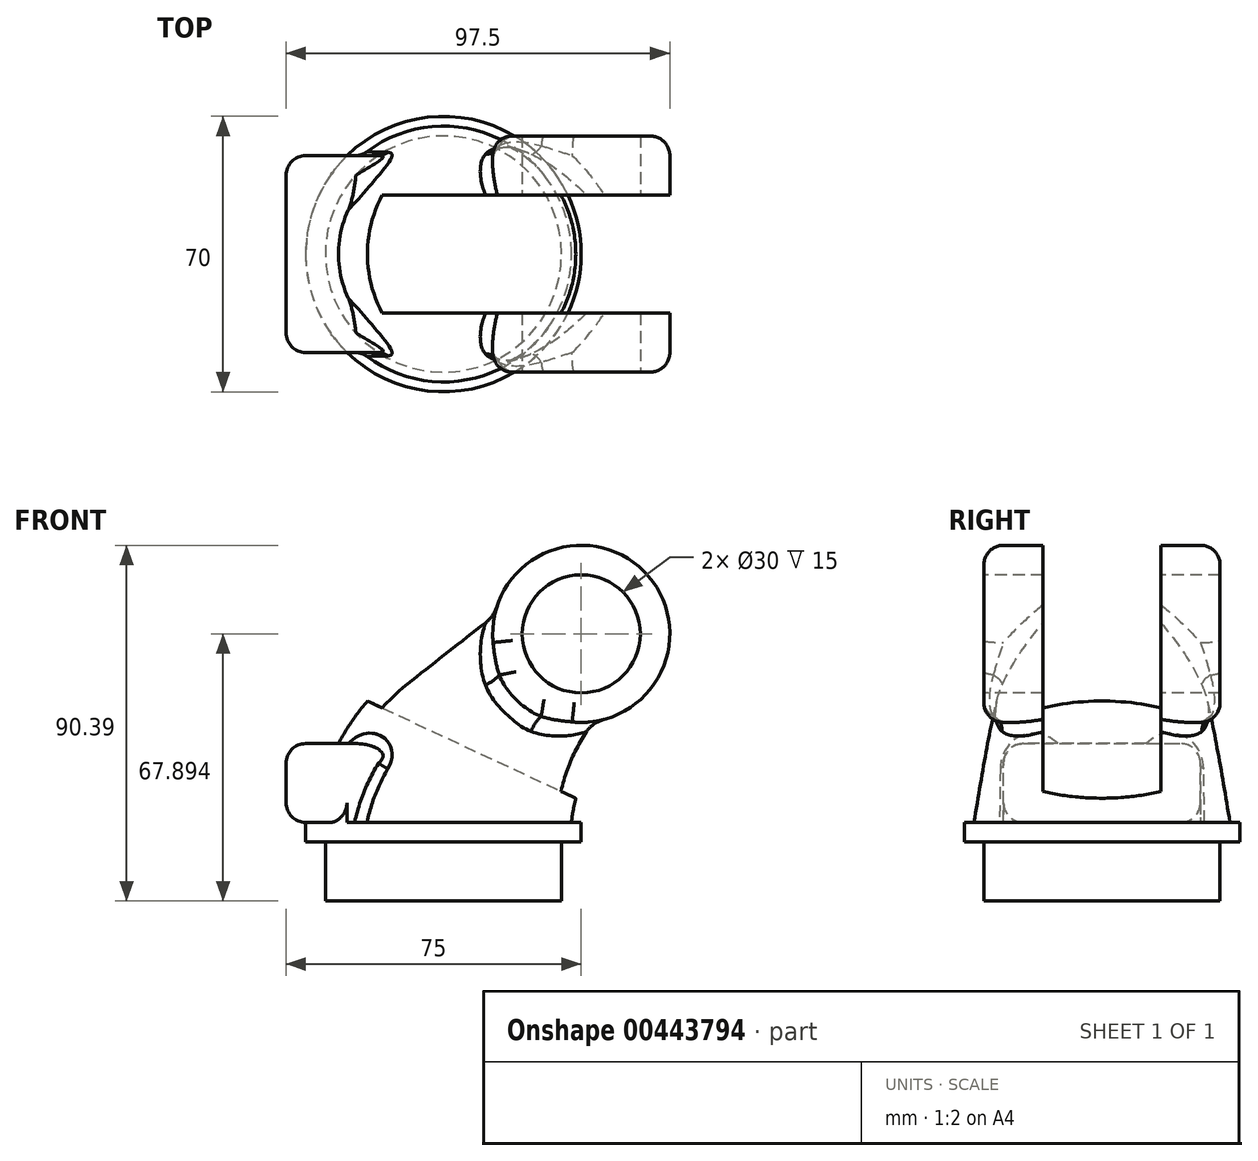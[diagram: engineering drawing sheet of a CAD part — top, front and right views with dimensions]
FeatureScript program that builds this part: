
annotation { "Feature Type Name" : "Feature", "Feature Type Description" : "" }
export const myFeature = defineFeature(function(context is Context, id is Id, definition is map)
    precondition{}
    {
        {
            var Q0;
            Q0=qCreatedBy(makeId("Top.planeOp"),FACE);
            var sketch = newSketch(context, id + "F0", { "sketchPlane" : qUnion([Q0])});
            skCircle(sketch, "E0", {"center": v(0, 0) * mm, "radius": 35 * mm});
            skSolve(sketch);
        }
        {
            var Q0;
            Q0 = qSketchRegion(id + "F0", true);
            extrude(context, id + "F1", {"entities" : qUnion([Q0]), "depth" : 5 * mm});
        }
        {
            var Q0;
            Q0=qCreatedBy(makeId("Front.planeOp"),FACE);
            var sketch = newSketch(context, id + "F2", { "sketchPlane" : qUnion([Q0])});
            skArc(sketch, "E1", {"start": v(17.6, 38.3) * mm, "mid": v(5.55, 23.37) * mm, "end": v(0, 5) * mm});
            skLineSegment(sketch, "E2", {"start": v(35, 52.9) * mm, "end": v(17.6, 38.3) * mm});
            skSolve(sketch);
        }
        {
            var Q0;
            Q0=sQuery(id+"F2.wireOp",EDGE,"E2");
            var Q1;
            Q1=sQuery(id+"F2.wireOp",VERTEX,"E2.start");
            cPlane(context, id + "F3", {"entities" : qUnion([Q0, Q1]), "cplaneType" : CPlaneType.LINE_POINT, "offset" : 25 * mm, "width" : 150 * mm, "height" : 150 * mm});
        }
        {
            var Q0;
            Q0=qCreatedBy(id+"F3.planeOp",FACE);
            var sketch = newSketch(context, id + "F4", { "sketchPlane" : qUnion([Q0])});
            skCircle(sketch, "E3", {"center": v(0, 18.02) * mm, "radius": 22.5 * mm});
            skSolve(sketch);
        }
        {
            var Q0;
            Q0=makeQuery(id+"F1.opExtrude","CAP_FACE",FACE,{"disambiguationData":[OSD([sQuery(id+"F0.wireOp",EDGE,"E0")])],"isStart":false});
            var sketch = newSketch(context, id + "F5", { "sketchPlane" : qUnion([Q0])});
            skCircle(sketch, "E4", {"center": v(0, 0) * mm, "radius": 32.5 * mm});
            skSolve(sketch);
        }
        {
            var Q0;
            Q0=qCreatedBy(makeId("Front.planeOp"),FACE);
            var sketch = newSketch(context, id + "F6", { "sketchPlane" : qUnion([Q0])});
            skArc(sketch, "E5", {"start": v(-13.25, 41.78) * mm, "mid": v(-26.5, 25.3) * mm, "end": v(-32.5, 5) * mm});
            skLineSegment(sketch, "E6", {"start": v(-13.25, 41.78) * mm, "end": v(20.54, 70.13) * mm});
            skSolve(sketch);
        }
        {
            var Q0;
            Q0=qCreatedBy(makeId("Front.planeOp"),FACE);
            var sketch = newSketch(context, id + "F7", { "sketchPlane" : qUnion([Q0])});
            skArc(sketch, "E7", {"start": v(48.46, 34.82) * mm, "mid": v(37.6, 21.45) * mm, "end": v(32.5, 5) * mm});
            skLineSegment(sketch, "E8", {"start": v(48.46, 34.82) * mm, "end": v(49.46, 35.66) * mm});
            skSolve(sketch);
        }
        {
            var Q1;
            Q1=makeQuery(id+"F5.imprint","IMPRINT",FACE,{"disambiguationData":[TD([[makeQuery(id+"F5.imprint","IMPRINT",EDGE,{"derivedFrom":sQuery(id+"F5.wireOp",EDGE,"E4")}),1.0]])]});
            var Q2;
            Q2=makeQuery(id+"F4.imprint","IMPRINT",FACE,{"disambiguationData":[TD([[makeQuery(id+"F4.imprint","IMPRINT",EDGE,{"derivedFrom":sQuery(id+"F4.wireOp",EDGE,"E3")}),1.0]])]});
            var Q3;
            Q3 = qConstructionFilter(qBodyType(qCreatedBy(id + "F7" ,EDGE), BodyType.WIRE), ConstructionObject.NO);
            var Q4;
            Q4 = qConstructionFilter(qBodyType(qCreatedBy(id + "F6" ,EDGE), BodyType.WIRE), ConstructionObject.NO);
            loft(context, id + "F8", {"operationType" : NewBodyOperationType.ADD, "addGuides" : true, "sheetProfilesArray" : [{ "sheetProfileEntities" : qUnion([Q1]) }, { "sheetProfileEntities" : qUnion([Q2]) }], "guidesArray" : [{ "guideEntities" : qUnion([Q3]), "guideDerivativeType" : LoftGuideDerivativeType.DEFAULT, "guideDerivativeMagnitude" : 1 }, { "guideEntities" : qUnion([Q4]), "guideDerivativeType" : LoftGuideDerivativeType.DEFAULT, "guideDerivativeMagnitude" : 1 }]});
        }
        {
            var Q0;
            Q0=qCreatedBy(makeId("Front.planeOp"),FACE);
            var sketch = newSketch(context, id + "F9", { "sketchPlane" : qUnion([Q0])});
            skCircle(sketch, "E9", {"center": v(35, 52.9) * mm, "radius": 22.5 * mm});
            skSolve(sketch);
        }
        {
            var Q0;
            Q0 = qSketchRegion(id + "F9", true);
            extrude(context, id + "F10", {"entities" : qUnion([Q0]), "operationType" : NewBodyOperationType.ADD, "endBound" : BoundingType.SYMMETRIC, "depth" : 60 * mm});
        }
        {
            var Q0;
            Q0=makeQuery(id+"F10.boolean.opBoolean","INTERSECT",EDGE,{"disambiguationData":[OD(1.0)],"derivedFrom":[makeQuery(id+"F8.opLoft","SWEPT_FACE",FACE,{"disambiguationData":[OSD([sQuery(id+"F4.wireOp",EDGE,"E3"),sQuery(id+"F5.wireOp",EDGE,"E4"),sQuery(id+"F6.wireOp",VERTEX,"E6.start"),sQuery(id+"F6.wireOp",EDGE,"E5"),sQuery(id+"F6.wireOp",EDGE,"E6"),sQuery(id+"F7.wireOp",VERTEX,"E8.start"),sQuery(id+"F7.wireOp",EDGE,"E7"),sQuery(id+"F7.wireOp",EDGE,"E8")])]}),makeQuery(id+"F10.opExtrude","SWEPT_FACE",FACE,{"disambiguationData":[OSD([sQuery(id+"F9.wireOp",EDGE,"E9")])]})]});
            var Q1;
            Q1=makeQuery(id+"F10.boolean.opBoolean","INTERSECT",EDGE,{"disambiguationData":[OD(0.0)],"derivedFrom":[makeQuery(id+"F8.opLoft","SWEPT_FACE",FACE,{"disambiguationData":[OSD([sQuery(id+"F4.wireOp",EDGE,"E3"),sQuery(id+"F5.wireOp",EDGE,"E4"),sQuery(id+"F6.wireOp",VERTEX,"E6.start"),sQuery(id+"F6.wireOp",EDGE,"E5"),sQuery(id+"F6.wireOp",EDGE,"E6"),sQuery(id+"F7.wireOp",VERTEX,"E8.start"),sQuery(id+"F7.wireOp",EDGE,"E7"),sQuery(id+"F7.wireOp",EDGE,"E8")])]}),makeQuery(id+"F10.opExtrude","SWEPT_FACE",FACE,{"disambiguationData":[OSD([sQuery(id+"F9.wireOp",EDGE,"E9")])]})]});
            fillet(context, id + "F11", {"entities" : qUnion([Q0, Q1]), "radius" : 5 * mm, "tangentPropagation" : true, "allowEdgeOverflow" : false});
        }
        {
            var Q0;
            Q0=makeQuery(id+"F10.opExtrude","CAP_EDGE",EDGE,{"disambiguationData":[OSD([sQuery(id+"F9.wireOp",EDGE,"E9")])],"isStart":false});
            var Q1;
            Q1=makeQuery(id+"F10.opExtrude","CAP_EDGE",EDGE,{"disambiguationData":[OSD([sQuery(id+"F9.wireOp",EDGE,"E9")])],"isStart":true});
            fillet(context, id + "F12", {"entities" : qUnion([Q0, Q1]), "radius" : 5 * mm, "tangentPropagation" : true, "allowEdgeOverflow" : false});
        }
        {
            var Q0;
            Q0=makeQuery(id+"F10.opExtrude","CAP_FACE",FACE,{"disambiguationData":[OSD([sQuery(id+"F9.wireOp",EDGE,"E9")])],"isStart":false});
            var sketch = newSketch(context, id + "F13", { "sketchPlane" : qUnion([Q0])});
            skCircle(sketch, "E10", {"center": v(35, 52.9) * mm, "radius": 15 * mm});
            skSolve(sketch);
        }
        {
            var Q0;
            Q0 = qSketchRegion(id + "F13", true);
            extrude(context, id + "F14", {"entities" : qUnion([Q0]), "operationType" : NewBodyOperationType.REMOVE, "endBound" : BoundingType.THROUGH_ALL, "oppositeDirection" : true, "depth" : 25 * mm});
        }
        {
            var Q0;
            Q0=qCreatedBy(makeId("Front.planeOp"),FACE);
            var sketch = newSketch(context, id + "F15", { "sketchPlane" : qUnion([Q0])});
            skLineSegment(sketch, "E11", {"start": v(-104.18, 75.4) * mm, "end": v(57.5, 0) * mm});
            skLineSegment(sketch, "E12", {"start": v(57.5, 75.4) * mm, "end": v(57.5, 0) * mm});
            skLineSegment(sketch, "E13", {"start": v(-104.18, 75.4) * mm, "end": v(57.5, 75.4) * mm});
            skSolve(sketch);
        }
        {
            var Q0;
            Q0 = qSketchRegion(id + "F15", true);
            extrude(context, id + "F16", {"entities" : qUnion([Q0]), "operationType" : NewBodyOperationType.REMOVE, "endBound" : BoundingType.SYMMETRIC, "oppositeDirection" : true, "depth" : 30 * mm});
        }
        {
            var Q0;
            Q0=qCreatedBy(makeId("Front.planeOp"),FACE);
            var sketch = newSketch(context, id + "F17", { "sketchPlane" : qUnion([Q0])});
            skLineSegment(sketch, "E14.bottom", {"start": v(0, 0) * mm, "end": v(-30, 0) * mm});
            skLineSegment(sketch, "E14.top", {"start": v(0, -15) * mm, "end": v(-30, -15) * mm});
            skLineSegment(sketch, "E14.left", {"start": v(0, 0) * mm, "end": v(0, -15) * mm});
            skLineSegment(sketch, "E14.right", {"start": v(-30, 0) * mm, "end": v(-30, -15) * mm});
            skSolve(sketch);
        }
        {
            var Q0;
            Q0 = qSketchRegion(id + "F17", true);
            var Q1;
            Q1=sQuery(id+"F17.wireOp",EDGE,"E14.left");
            revolve(context, id + "F18", {"operationType" : NewBodyOperationType.ADD, "entities" : qUnion([Q0]), "axis" : qUnion([Q1]), "revolveType" : RevolveType.FULL});
        }
        {
            var Q0;
            Q0=qCreatedBy(makeId("Right.planeOp"),FACE);
            var sketch = newSketch(context, id + "F19", { "sketchPlane" : qUnion([Q0])});
            skLineSegment(sketch, "E15.bottom", {"start": v(-25, 5) * mm, "end": v(25, 5) * mm});
            skLineSegment(sketch, "E15.top", {"start": v(-25, 25) * mm, "end": v(25, 25) * mm});
            skLineSegment(sketch, "E15.left", {"start": v(-25, 5) * mm, "end": v(-25, 25) * mm});
            skLineSegment(sketch, "E15.right", {"start": v(25, 5) * mm, "end": v(25, 25) * mm});
            skPoint(sketch, "E15.middle", {"position": v(0, 15) * mm});
            skSolve(sketch);
        }
        {
            var Q0;
            Q0 = qSketchRegion(id + "F19", true);
            extrude(context, id + "F20", {"entities" : qUnion([Q0]), "operationType" : NewBodyOperationType.ADD, "oppositeDirection" : true, "depth" : 40 * mm});
        }
        {
            var Q0;
            Q0=makeQuery(id+"F20.opExtrude","SWEPT_EDGE",EDGE,{"disambiguationData":[OSD([sQuery(id+"F19.wireOp",EDGE,"E15.top"),sQuery(id+"F19.wireOp",EDGE,"E15.left")])]});
            var Q1;
            Q1=makeQuery(id+"F20.opExtrude","CAP_EDGE",EDGE,{"disambiguationData":[OSD([sQuery(id+"F19.wireOp",EDGE,"E15.left")])],"isStart":false});
            var Q2;
            {var subQ0=sQuery(id+"F19.wireOp",EDGE,"E15.bottom");var subQ1=sQuery(id+"F19.wireOp",EDGE,"E15.left");Q2=makeQuery(id+"F20.boolean.opBoolean","SPLIT",EDGE,{"disambiguationData":[topologyDisambiguationEdgeConnected([makeQuery(id+"F20.opExtrude","SWEPT_FACE",FACE,{"disambiguationData":[OSD([subQ0])]})])],"derivedFrom":makeQuery(id+"F20.opExtrude","SWEPT_EDGE",EDGE,{"disambiguationData":[OSD([subQ0,subQ1])]})});}
            var Q3;
            Q3=makeQuery(id+"F20.boolean.opBoolean","INTERSECT",EDGE,{"derivedFrom":[makeQuery(id+"F8.opLoft","SWEPT_FACE",FACE,{"disambiguationData":[OSD([sQuery(id+"F4.wireOp",EDGE,"E3"),sQuery(id+"F5.wireOp",EDGE,"E4"),sQuery(id+"F6.wireOp",VERTEX,"E6.start"),sQuery(id+"F6.wireOp",EDGE,"E5"),sQuery(id+"F6.wireOp",EDGE,"E6"),sQuery(id+"F7.wireOp",VERTEX,"E8.start"),sQuery(id+"F7.wireOp",EDGE,"E7"),sQuery(id+"F7.wireOp",EDGE,"E8")])]}),makeQuery(id+"F20.opExtrude","SWEPT_FACE",FACE,{"disambiguationData":[OSD([sQuery(id+"F19.wireOp",EDGE,"E15.left")])]})]});
            var Q4;
            Q4=makeQuery(id+"F20.opExtrude","CAP_EDGE",EDGE,{"disambiguationData":[OSD([sQuery(id+"F19.wireOp",EDGE,"E15.top")])],"isStart":false});
            var Q5;
            Q5=makeQuery(id+"F20.opExtrude","CAP_EDGE",EDGE,{"disambiguationData":[OSD([sQuery(id+"F19.wireOp",EDGE,"E15.bottom")])],"isStart":false});
            var Q6;
            Q6=makeQuery(id+"F20.opExtrude","CAP_EDGE",EDGE,{"disambiguationData":[OSD([sQuery(id+"F19.wireOp",EDGE,"E15.right")])],"isStart":false});
            var Q7;
            Q7=makeQuery(id+"F20.opExtrude","SWEPT_EDGE",EDGE,{"disambiguationData":[OSD([sQuery(id+"F19.wireOp",EDGE,"E15.top"),sQuery(id+"F19.wireOp",EDGE,"E15.right")])]});
            var Q8;
            {var subQ0=sQuery(id+"F19.wireOp",EDGE,"E15.bottom");var subQ1=sQuery(id+"F19.wireOp",EDGE,"E15.right");Q8=makeQuery(id+"F20.boolean.opBoolean","SPLIT",EDGE,{"disambiguationData":[topologyDisambiguationEdgeConnected([makeQuery(id+"F20.opExtrude","SWEPT_FACE",FACE,{"disambiguationData":[OSD([subQ0])]})])],"derivedFrom":makeQuery(id+"F20.opExtrude","SWEPT_EDGE",EDGE,{"disambiguationData":[OSD([subQ0,subQ1])]})});}
            var Q9;
            Q9=makeQuery(id+"F20.boolean.opBoolean","INTERSECT",EDGE,{"derivedFrom":[makeQuery(id+"F8.opLoft","SWEPT_FACE",FACE,{"disambiguationData":[OSD([sQuery(id+"F4.wireOp",EDGE,"E3"),sQuery(id+"F5.wireOp",EDGE,"E4"),sQuery(id+"F6.wireOp",VERTEX,"E6.start"),sQuery(id+"F6.wireOp",EDGE,"E5"),sQuery(id+"F6.wireOp",EDGE,"E6"),sQuery(id+"F7.wireOp",VERTEX,"E8.start"),sQuery(id+"F7.wireOp",EDGE,"E7"),sQuery(id+"F7.wireOp",EDGE,"E8")])]}),makeQuery(id+"F20.opExtrude","SWEPT_FACE",FACE,{"disambiguationData":[OSD([sQuery(id+"F19.wireOp",EDGE,"E15.right")])]})]});
            fillet(context, id + "F21", {"entities" : qUnion([Q0, Q1, Q2, Q3, Q4, Q5, Q6, Q7, Q8, Q9]), "radius" : 5 * mm, "tangentPropagation" : true, "allowEdgeOverflow" : false});
        }
    });
